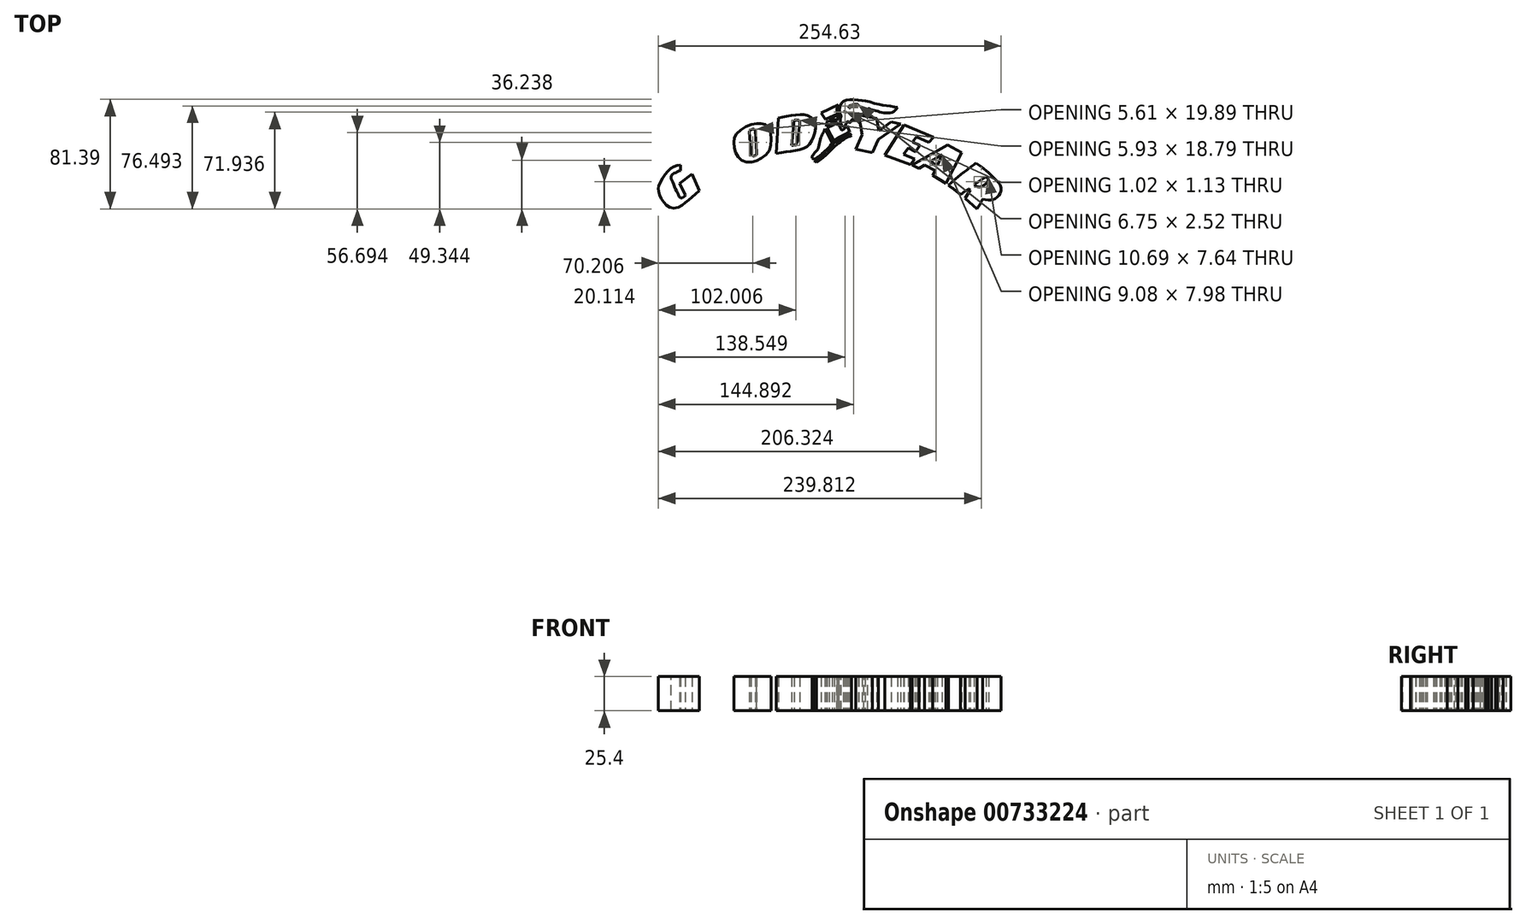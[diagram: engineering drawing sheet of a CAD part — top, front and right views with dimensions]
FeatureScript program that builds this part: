
annotation { "Feature Type Name" : "Feature", "Feature Type Description" : "" }
export const myFeature = defineFeature(function(context is Context, id is Id, definition is map)
    precondition{}
    {
        {
            var Q0;
            Q0=qCreatedBy(makeId("Top.planeOp"),FACE);
            var sketch = newSketch(context, id + "F0", { "sketchPlane" : qUnion([Q0])});
            skFitSpline(sketch, "E0", {"points": [v(-59.77, 19.65) * mm, v(-63.83, 18.9) * mm, v(-66.56, 17.29) * mm, v(-70.08, 14) * mm, v(-73.2, 9.83) * mm, v(-75.73, 4.75) * mm, v(-76.25, 2.47) * mm, v(-76.18, 0) * mm, v(-74.98, -3.55) * mm, v(-72.37, -7.96) * mm, v(-69.17, -11.16) * mm, v(-64.56, -12.56) * mm, v(-59.15, -10.76) * mm, v(-55.35, -7.59) * mm, v(-51.14, -3.95) * mm, v(-45.8, 0.36) * mm], "startDerivative": vector(-48.72, 2.07) * mm, "endDerivative": vector(63.75, 50.3) * mm});
            skLineSegment(sketch, "E1", {"start": v(-59.77, 19.65) * mm, "end": v(-59.86, 15.48) * mm});
            skLineSegment(sketch, "E2", {"start": v(-45.8, 0.36) * mm, "end": v(-51.25, 12.96) * mm});
            skLineSegment(sketch, "E3", {"start": v(-51.25, 12.96) * mm, "end": v(-60.63, 5.88) * mm});
            skLineSegment(sketch, "E4", {"start": v(-60.63, 5.88) * mm, "end": v(-56.41, -2.7) * mm});
            skFitSpline(sketch, "E5", {"points": [v(-59.86, 15.48) * mm, v(-62.4, 14.45) * mm, v(-64.42, 13.43) * mm, v(-66.28, 12.15) * mm, v(-66.87, 9.93) * mm, v(-66.03, 7.47) * mm, v(-64, 2.8) * mm, v(-62.32, -0.84) * mm, v(-61.06, -3.39) * mm, v(-60.55, -4.32) * mm, v(-58.95, -4.91) * mm, v(-57.09, -4.06) * mm, v(-56.41, -2.7) * mm], "startDerivative": vector(-29.78, -11.35) * mm, "endDerivative": vector(6.97, 21.82) * mm});
            skFitSpline(sketch, "E6", {"points": [v(-39.36, 28.04) * mm, v(-39.36, 30.3) * mm, v(-36.88, 32.38) * mm, v(-36.05, 31.72) * mm], "startDerivative": vector(-0.89, 7.93) * mm, "endDerivative": vector(3.61, -4.33) * mm});
            skLineSegment(sketch, "E7", {"start": v(-8.9, 44.2) * mm, "end": v(-7.35, 27.45) * mm});
            skLineSegment(sketch, "E8", {"start": v(-4.4, 45.2) * mm, "end": v(-3.4, 28.77) * mm});
            skFitSpline(sketch, "E9", {"points": [v(-8.9, 44.2) * mm, v(-8.13, 45.2) * mm, v(-6.65, 46.05) * mm, v(-5.18, 46.05) * mm, v(-4.4, 45.2) * mm], "startDerivative": vector(2.8, 4.36) * mm, "endDerivative": vector(2.83, -4.51) * mm});
            skFitSpline(sketch, "E10", {"points": [v(-7.35, 27.45) * mm, v(-6.5, 26.52) * mm, v(-5.65, 26.29) * mm, v(-4.64, 26.44) * mm, v(-3.4, 27.3) * mm, v(-3.4, 28.77) * mm], "startDerivative": vector(3.78, -5) * mm, "endDerivative": vector(-0.95, 4.32) * mm});
            skFitSpline(sketch, "E11", {"points": [v(-18.2, 42.64) * mm, v(-12.62, 47.37) * mm, v(-6.27, 49.93) * mm, v(-1.3, 50.4) * mm, v(2.34, 49.85) * mm, v(5.9, 47.3) * mm, v(7.53, 39.7) * mm, v(6.83, 32.33) * mm, v(4.12, 27.53) * mm, v(-1.46, 23.89) * mm, v(-6.11, 21.87) * mm, v(-12.23, 22.1) * mm, v(-16.34, 24.5) * mm, v(-18.82, 28.46) * mm, v(-20.22, 33.88) * mm, v(-19.9, 39.39) * mm, v(-18.2, 42.64) * mm]});
            skLineSegment(sketch, "E12", {"start": v(11.4, 28.26) * mm, "end": v(12.75, 54.33) * mm});
            skFitSpline(sketch, "E13", {"points": [v(12.75, 54.33) * mm, v(20.03, 55.86) * mm, v(28.5, 57.04) * mm, v(34.08, 56.36) * mm, v(39.5, 52.64) * mm, v(40.17, 45.53) * mm, v(38.14, 38.42) * mm, v(34.59, 33.68) * mm, v(28.83, 31.14) * mm, v(21.05, 29.62) * mm, v(11.4, 28.26) * mm], "startDerivative": vector(68.9, 15.11) * mm, "endDerivative": vector(-84.89, -11.4) * mm});
            skLineSegment(sketch, "E14", {"start": v(24.6, 52.98) * mm, "end": v(22.74, 34.19) * mm});
            skFitSpline(sketch, "E15", {"points": [v(24.6, 52.98) * mm, v(27.14, 52.98) * mm, v(28.44, 52.5) * mm, v(28.64, 50.15) * mm, v(27.66, 41.03) * mm, v(26.74, 36.1) * mm, v(26.16, 35.14) * mm, v(25.17, 34.46) * mm, v(22.74, 34.19) * mm], "startDerivative": vector(22.33, 0.87) * mm, "endDerivative": vector(-23, -0.54) * mm});
            skFitSpline(sketch, "E16", {"points": [v(39.1, 23.6) * mm, v(44.18, 27) * mm, v(48.7, 31.12) * mm, v(50.89, 33.22) * mm, v(51.7, 34.88) * mm, v(52.92, 36) * mm], "startDerivative": vector(19.7, 11.7) * mm, "endDerivative": vector(13.38, 3.84) * mm});
            skLineSegment(sketch, "E17", {"start": v(47.46, 46.57) * mm, "end": v(52.92, 36) * mm});
            skFitSpline(sketch, "E18", {"points": [v(47.46, 46.57) * mm, v(46.54, 44.19) * mm, v(45.11, 41.5) * mm, v(43.53, 37) * mm, v(42.43, 32.07) * mm, v(39.8, 28.44) * mm, v(38.07, 26.31) * mm, v(37.96, 24.84) * mm, v(39.1, 23.6) * mm], "startDerivative": vector(-7.2, -21.21) * mm, "endDerivative": vector(15.31, -12.42) * mm});
            skLineSegment(sketch, "E19", {"start": v(40.96, 21.31) * mm, "end": v(39.53, 22.69) * mm});
            skLineSegment(sketch, "E20", {"start": v(65.88, 43.08) * mm, "end": v(67.2, 41.3) * mm});
            skFitSpline(sketch, "E21", {"points": [v(65.88, 43.08) * mm, v(64.37, 42.22) * mm, v(62.42, 41.22) * mm, v(59.63, 39.5) * mm, v(56.94, 37.62) * mm, v(53.71, 35.18) * mm, v(48.96, 30.47) * mm, v(47.97, 29.32) * mm, v(46.11, 27.54) * mm, v(43.82, 25.45) * mm, v(41.44, 24.06) * mm, v(39.53, 22.69) * mm], "startDerivative": vector(-17.38, -20) * mm, "endDerivative": vector(-22.35, -17.46) * mm});
            skFitSpline(sketch, "E22", {"points": [v(67.2, 41.3) * mm, v(66, 40.84) * mm, v(64.5, 40.51) * mm, v(62.4, 39.36) * mm, v(58.05, 36.12) * mm, v(53.94, 32.64) * mm, v(49.63, 28.21) * mm, v(46.94, 25.96) * mm, v(44.17, 23.59) * mm, v(40.96, 21.31) * mm], "startDerivative": vector(-16.72, -16.2) * mm, "endDerivative": vector(-28.08, -18.76) * mm});
            skLineSegment(sketch, "E23", {"start": v(47.81, 53.38) * mm, "end": v(44.5, 58.28) * mm});
            skLineSegment(sketch, "E24", {"start": v(44.5, 58.28) * mm, "end": v(57.43, 64.4) * mm});
            skLineSegment(sketch, "E25", {"start": v(47.81, 53.38) * mm, "end": v(57.06, 57.79) * mm});
            skFitSpline(sketch, "E26", {"points": [v(57.43, 64.4) * mm, v(56.51, 62.01) * mm, v(56.51, 59.2) * mm, v(57.06, 57.79) * mm], "startDerivative": vector(-3.12, -6.33) * mm, "endDerivative": vector(2.33, -4.57) * mm});
            skLineSegment(sketch, "E27", {"start": v(50.63, 53.74) * mm, "end": v(57.69, 57.09) * mm});
            skLineSegment(sketch, "E28", {"start": v(50.63, 53.74) * mm, "end": v(57.3, 53.2) * mm});
            skFitSpline(sketch, "E29", {"points": [v(57.69, 57.09) * mm, v(57.17, 55.72) * mm, v(57.3, 53.2) * mm], "startDerivative": vector(-2.15, -4.28) * mm, "endDerivative": vector(1.5, -3.48) * mm});
            skLineSegment(sketch, "E30", {"start": v(48.55, 48.32) * mm, "end": v(49.17, 52.19) * mm});
            skLineSegment(sketch, "E31", {"start": v(49.17, 52.19) * mm, "end": v(56.3, 51.91) * mm});
            skLineSegment(sketch, "E32", {"start": v(48.55, 48.32) * mm, "end": v(56.3, 51.91) * mm});
            skLineSegment(sketch, "E33", {"start": v(48.94, 47.29) * mm, "end": v(54.3, 36.9) * mm});
            skLineSegment(sketch, "E34", {"start": v(48.94, 47.29) * mm, "end": v(57.19, 51.08) * mm});
            skLineSegment(sketch, "E35", {"start": v(57.19, 51.08) * mm, "end": v(58.36, 48.52) * mm});
            skFitSpline(sketch, "E36", {"points": [v(58.36, 48.52) * mm, v(59.08, 46.84) * mm, v(59.66, 45.79) * mm, v(61.14, 45.98) * mm, v(63.83, 48.86) * mm], "startDerivative": vector(3.27, -7.15) * mm, "endDerivative": vector(7.57, 10.06) * mm});
            skLineSegment(sketch, "E37", {"start": v(63.83, 48.86) * mm, "end": v(65.82, 44.11) * mm});
            skFitSpline(sketch, "E38", {"points": [v(54.3, 36.9) * mm, v(55.69, 38.57) * mm, v(60.65, 41.48) * mm, v(65.82, 44.11) * mm], "startDerivative": vector(4.45, 7) * mm, "endDerivative": vector(13.02, 6.62) * mm});
            skFitSpline(sketch, "E39", {"points": [v(61.18, 48.14) * mm, v(59.75, 49.36) * mm, v(58.81, 53.55) * mm, v(59.36, 56.2) * mm, v(58.43, 58.46) * mm, v(58.43, 62.76) * mm, v(60.3, 66.01) * mm, v(63.28, 67.89) * mm, v(68.08, 68.22) * mm, v(73.92, 67.61) * mm, v(78.94, 66.95) * mm, v(86.83, 64.74) * mm, v(91.57, 63.97) * mm, v(97.08, 63.03) * mm, v(101.33, 62.43) * mm], "startDerivative": vector(-31.99, 17.8) * mm, "endDerivative": vector(56.5, -7.36) * mm});
            skFitSpline(sketch, "E40", {"points": [v(101.33, 62.43) * mm, v(98.46, 59.34) * mm, v(94.1, 58.18) * mm, v(88.87, 58.9) * mm, v(84.12, 60.28) * mm, v(81.15, 61.1) * mm, v(79.88, 61.54) * mm, v(79.16, 60.94) * mm, v(79.71, 60.39) * mm, v(80.65, 59.9) * mm, v(81.75, 59.72) * mm], "startDerivative": vector(-19.3, -26.52) * mm, "endDerivative": vector(16.87, -1.16) * mm});
            skFitSpline(sketch, "E41", {"points": [v(81.75, 59.72) * mm, v(79.88, 58.68) * mm, v(78, 58.73) * mm, v(76.46, 58.95) * mm, v(76.4, 58.24) * mm, v(77.18, 57.85) * mm], "startDerivative": vector(-7.43, -5.2) * mm, "endDerivative": vector(5.92, -1.38) * mm});
            skFitSpline(sketch, "E42", {"points": [v(77.18, 57.85) * mm, v(76.35, 57.32) * mm, v(74.43, 57.29) * mm, v(72.68, 57.62) * mm, v(70.63, 57.45) * mm, v(70.2, 54.94) * mm, v(69.4, 53.45) * mm, v(67.58, 53.5) * mm, v(66.48, 51.67) * mm, v(65.59, 51) * mm, v(64.36, 51.84) * mm, v(63.05, 50.4) * mm, v(62.37, 48.62) * mm, v(61.18, 48.14) * mm], "startDerivative": vector(-11.9, -10.87) * mm, "endDerivative": vector(-16.98, 9.93) * mm});
            skFitSpline(sketch, "E43", {"points": [v(61.74, 59.24) * mm, v(62.63, 59.24) * mm, v(62.65, 58.37) * mm, v(62.19, 58.35) * mm, v(62.32, 58.84) * mm, v(61.9, 58.82) * mm, v(61.74, 59.24) * mm]});
            skFitSpline(sketch, "E44", {"points": [v(65.21, 62.9) * mm, v(66.4, 63.76) * mm, v(68.44, 64.34) * mm, v(70.3, 64.56) * mm, v(71.94, 64.47) * mm, v(71.87, 63.65) * mm, v(69.29, 63.25) * mm, v(66.9, 62.78) * mm, v(66.02, 62.18) * mm, v(65.15, 62.25) * mm, v(65.21, 62.9) * mm]});
            skLineSegment(sketch, "E45", {"start": v(72.66, 56.7) * mm, "end": v(75.06, 41.97) * mm});
            skLineSegment(sketch, "E46", {"start": v(75.06, 41.97) * mm, "end": v(70.23, 31.2) * mm});
            skLineSegment(sketch, "E47", {"start": v(70.23, 31.2) * mm, "end": v(82.54, 28.69) * mm});
            skLineSegment(sketch, "E48", {"start": v(82.54, 28.69) * mm, "end": v(87, 38.62) * mm});
            skLineSegment(sketch, "E49", {"start": v(87, 38.62) * mm, "end": v(103.68, 50.06) * mm});
            skLineSegment(sketch, "E50", {"start": v(103.68, 50.06) * mm, "end": v(96.8, 51.47) * mm});
            skLineSegment(sketch, "E51", {"start": v(96.8, 51.47) * mm, "end": v(87.33, 44.97) * mm});
            skLineSegment(sketch, "E52", {"start": v(87.33, 44.97) * mm, "end": v(85.86, 54) * mm});
            skLineSegment(sketch, "E53", {"start": v(85.86, 54) * mm, "end": v(72.66, 56.7) * mm});
            skLineSegment(sketch, "E54", {"start": v(91.9, 26.82) * mm, "end": v(106.1, 49.42) * mm});
            skLineSegment(sketch, "E55", {"start": v(106.1, 49.42) * mm, "end": v(128.08, 40.3) * mm});
            skLineSegment(sketch, "E56", {"start": v(128.08, 40.3) * mm, "end": v(124.49, 36.46) * mm});
            skLineSegment(sketch, "E57", {"start": v(124.49, 36.46) * mm, "end": v(115.55, 40.57) * mm});
            skLineSegment(sketch, "E58", {"start": v(115.55, 40.57) * mm, "end": v(112.49, 36.8) * mm});
            skLineSegment(sketch, "E59", {"start": v(112.49, 36.8) * mm, "end": v(118.1, 34.18) * mm});
            skLineSegment(sketch, "E60", {"start": v(118.1, 34.18) * mm, "end": v(114.68, 29.54) * mm});
            skLineSegment(sketch, "E61", {"start": v(114.68, 29.54) * mm, "end": v(109.42, 32.16) * mm});
            skLineSegment(sketch, "E62", {"start": v(109.42, 32.16) * mm, "end": v(105.74, 27.43) * mm});
            skLineSegment(sketch, "E63", {"start": v(105.74, 27.43) * mm, "end": v(114.15, 24.02) * mm});
            skLineSegment(sketch, "E64", {"start": v(114.15, 24.02) * mm, "end": v(110.82, 20) * mm});
            skLineSegment(sketch, "E65", {"start": v(110.82, 20) * mm, "end": v(91.9, 26.82) * mm});
            skLineSegment(sketch, "E66", {"start": v(112.29, 19.53) * mm, "end": v(138.65, 34.6) * mm});
            skLineSegment(sketch, "E67", {"start": v(138.65, 34.6) * mm, "end": v(149.02, 28.7) * mm});
            skLineSegment(sketch, "E68", {"start": v(149.02, 28.7) * mm, "end": v(137.16, 5.95) * mm});
            skLineSegment(sketch, "E69", {"start": v(137.16, 5.95) * mm, "end": v(127.55, 11.85) * mm});
            skLineSegment(sketch, "E70", {"start": v(127.55, 11.85) * mm, "end": v(129.33, 15.35) * mm});
            skLineSegment(sketch, "E71", {"start": v(129.33, 15.35) * mm, "end": v(121.52, 19.59) * mm});
            skLineSegment(sketch, "E72", {"start": v(121.52, 19.59) * mm, "end": v(117.2, 16.87) * mm});
            skLineSegment(sketch, "E73", {"start": v(117.2, 16.87) * mm, "end": v(112.29, 19.53) * mm});
            skLineSegment(sketch, "E74", {"start": v(125.49, 22.15) * mm, "end": v(134.56, 27.12) * mm});
            skLineSegment(sketch, "E75", {"start": v(134.56, 27.12) * mm, "end": v(131.04, 19.14) * mm});
            skLineSegment(sketch, "E76", {"start": v(131.04, 19.14) * mm, "end": v(125.49, 22.15) * mm});
            skFitSpline(sketch, "E77", {"points": [v(139.14, 4.57) * mm, v(145.18, 9.89) * mm, v(153.62, 16.45) * mm, v(159.77, 20.93) * mm], "startDerivative": vector(17.67, 16.08) * mm, "endDerivative": vector(18.73, 13.48) * mm});
            skFitSpline(sketch, "E78", {"points": [v(159.77, 20.93) * mm, v(168.42, 14.37) * mm, v(174.98, 7.8) * mm, v(178.1, 3.84) * mm, v(177.07, -2.4) * mm, v(172.06, -6.16) * mm, v(164.56, -5.74) * mm], "startDerivative": vector(44.5, -30.97) * mm, "endDerivative": vector(-46.73, 8.55) * mm});
            skFitSpline(sketch, "E79", {"points": [v(164.56, -5.74) * mm, v(162.69, -9.4) * mm, v(160.38, -13.1) * mm], "startDerivative": vector(-3.62, -7.3) * mm, "endDerivative": vector(-4.1, -6.66) * mm});
            skFitSpline(sketch, "E80", {"points": [v(139.14, 4.57) * mm, v(143.4, 1.34) * mm, v(148.2, -2.4) * mm], "startDerivative": vector(8.71, -6.53) * mm, "endDerivative": vector(9.4, -7.42) * mm});
            skFitSpline(sketch, "E81", {"points": [v(148.2, -2.4) * mm, v(150.73, -0.48) * mm, v(154.35, 1.86) * mm], "startDerivative": vector(4.88, 2.85) * mm, "endDerivative": vector(7.3, 5.55) * mm});
            skLineSegment(sketch, "E82", {"start": v(154.35, 1.86) * mm, "end": v(155.3, 1.04) * mm});
            skLineSegment(sketch, "E83", {"start": v(155.3, 1.04) * mm, "end": v(151.65, -5.27) * mm});
            skLineSegment(sketch, "E84", {"start": v(151.65, -5.27) * mm, "end": v(160.38, -13.1) * mm});
            skLineSegment(sketch, "E85", {"start": v(158.17, 4.93) * mm, "end": v(167, 10.82) * mm});
            skFitSpline(sketch, "E86", {"points": [v(167, 10.82) * mm, v(168.9, 9.08) * mm, v(167.83, 6.42) * mm, v(164.02, 3.8) * mm, v(161.31, 3.23) * mm, v(158.17, 4.93) * mm], "startDerivative": vector(14.19, -8.55) * mm, "endDerivative": vector(-15.28, 10.77) * mm});
            skSolve(sketch);
        }
        {
            var Q0;
            Q0=qSketchRegion(id+"F0",true);
            extrude(context, id + "F1", {"entities" : qUnion([Q0]), "depth" : 25.4 * mm, "offsetDistance" : 25.4 * mm});
        }
    });
